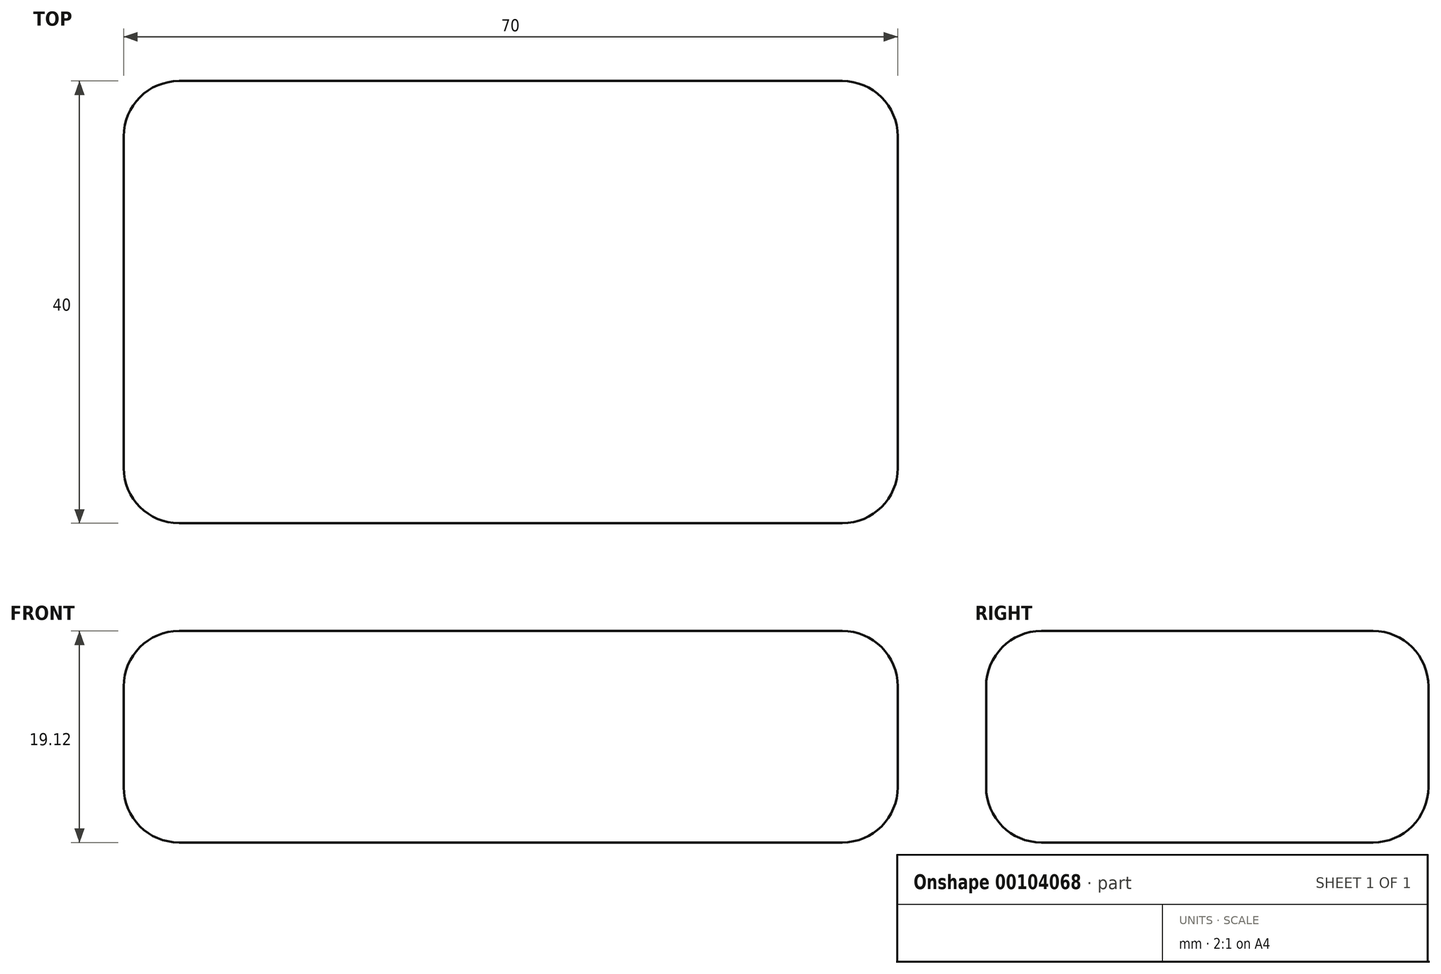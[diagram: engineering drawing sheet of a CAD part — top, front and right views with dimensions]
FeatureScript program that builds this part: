
annotation { "Feature Type Name" : "Feature", "Feature Type Description" : "" }
export const myFeature = defineFeature(function(context is Context, id is Id, definition is map)
    precondition{}
    {
        {
            var Q0;
            Q0=qCreatedBy(makeId("Front.planeOp"),FACE);
            var sketch = newSketch(context, id + "F0", { "sketchPlane" : qUnion([Q0])});
            skLineSegment(sketch, "E0.bottom", {"start": v(-66.69, 15) * mm, "end": v(-6.69, 15) * mm});
            skLineSegment(sketch, "E0.top", {"start": v(-66.69, -4.12) * mm, "end": v(-6.69, -4.12) * mm});
            skLineSegment(sketch, "E0.left", {"start": v(-71.69, 10) * mm, "end": v(-71.69, 0.88) * mm});
            skLineSegment(sketch, "E0.right", {"start": v(-1.69, 10) * mm, "end": v(-1.69, 0.88) * mm});
            skPoint(sketch, "E1.visualSharp", {"position": v(-71.69, 15) * mm});
            skArc(sketch, "E1.filletArc", {"start": v(-66.69, 15) * mm, "mid": v(-70.22, 13.54) * mm, "end": v(-71.69, 10) * mm});
            skPoint(sketch, "E2.visualSharp", {"position": v(-71.69, -4.12) * mm});
            skArc(sketch, "E2.filletArc", {"start": v(-71.69, 0.88) * mm, "mid": v(-70.22, -2.66) * mm, "end": v(-66.69, -4.12) * mm});
            skPoint(sketch, "E3.visualSharp", {"position": v(-1.69, 15) * mm});
            skArc(sketch, "E3.filletArc", {"start": v(-1.69, 10) * mm, "mid": v(-3.15, 13.54) * mm, "end": v(-6.69, 15) * mm});
            skPoint(sketch, "E4.visualSharp", {"position": v(-1.69, -4.12) * mm});
            skArc(sketch, "E4.filletArc", {"start": v(-6.69, -4.12) * mm, "mid": v(-3.15, -2.66) * mm, "end": v(-1.69, 0.88) * mm});
            skSolve(sketch);
        }
        {
            var Q0;
            Q0=makeQuery(id+"F0.imprint","IMPRINT",FACE,{"disambiguationData":[TD([[makeQuery(id+"F0.imprint","IMPRINT",EDGE,{"derivedFrom":sQuery(id+"F0.wireOp",EDGE,"E0.bottom")}),-1.0]])]});
            extrude(context, id + "F1", {"entities" : qUnion([Q0]), "depth" : 40 * mm});
        }
        {
            var Q0;
            Q0=makeQuery(id+"F1.opExtrude","CAP_EDGE",EDGE,{"disambiguationData":[OSD([sQuery(id+"F0.wireOp",EDGE,"E2.filletArc")])],"isStart":true});
            var Q1;
            Q1=makeQuery(id+"F1.opExtrude","SWEPT_FACE",FACE,{"disambiguationData":[OSD([sQuery(id+"F0.wireOp",EDGE,"E0.bottom")])]});
            fillet(context, id + "F2", {"entities" : qUnion([Q0, Q1]), "radius" : 5 * mm, "tangentPropagation" : true, "allowEdgeOverflow" : false});
        }
    });
